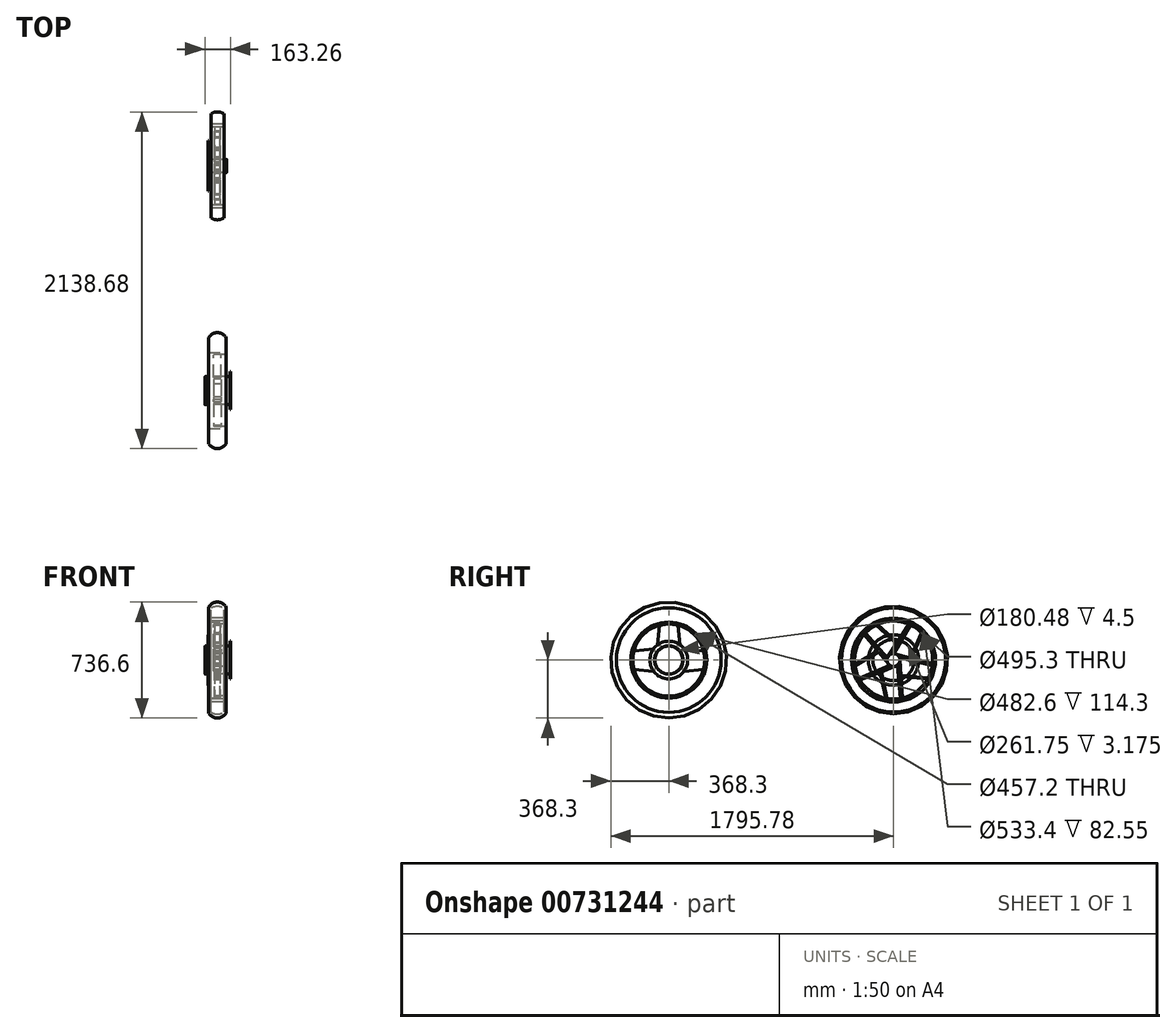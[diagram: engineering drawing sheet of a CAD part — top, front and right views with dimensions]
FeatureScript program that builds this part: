
annotation { "Feature Type Name" : "Feature", "Feature Type Description" : "" }
export const myFeature = defineFeature(function(context is Context, id is Id, definition is map)
    precondition{}
    {
        {
            var Q0;
            Q0=qCreatedBy(makeId("Right.planeOp"),FACE);
            var sketch = newSketch(context, id + "F0", { "sketchPlane" : qUnion([Q0])});
            skCircle(sketch, "E0", {"center": v(0, 0) * mm, "radius": 247.65 * mm});
            skCircle(sketch, "E1", {"center": v(0, 0) * mm, "radius": 41.28 * mm});
            skLineSegment(sketch, "E2", {"start": v(55.3, -241.4) * mm, "end": v(47.4, -104.93) * mm});
            skLineSegment(sketch, "E3", {"start": v(46.96, -97.18) * mm, "end": v(219.73, -114.22) * mm});
            skLineSegment(sketch, "E4.1.0", {"start": v(246.67, -22) * mm, "end": v(114.45, 12.66) * mm});
            skLineSegment(sketch, "E4.1.1", {"start": v(106.93, 14.63) * mm, "end": v(176.54, 173.68) * mm});
            skLineSegment(sketch, "E4.2.0", {"start": v(97.16, 227.8) * mm, "end": v(23.33, 112.76) * mm});
            skLineSegment(sketch, "E4.2.1", {"start": v(19.13, 106.22) * mm, "end": v(-110.63, 221.57) * mm});
            skLineSegment(sketch, "E4.3.0", {"start": v(-186.62, 162.8) * mm, "end": v(-100.03, 57.03) * mm});
            skLineSegment(sketch, "E4.3.1", {"start": v(-95.1, 51.01) * mm, "end": v(-244.9, -36.75) * mm});
            skLineSegment(sketch, "E4.4.0", {"start": v(-212.5, -127.18) * mm, "end": v(-85.15, -77.51) * mm});
            skLineSegment(sketch, "E4.4.1", {"start": v(-77.9, -74.7) * mm, "end": v(-40.73, -244.28) * mm});
            skLineSegment(sketch, "E5", {"start": v(43.26, -243.84) * mm, "end": v(23.46, -33.96) * mm});
            skLineSegment(sketch, "E6", {"start": v(47.4, -104.93) * mm, "end": v(215.77, -121.55) * mm});
            skLineSegment(sketch, "E7.1.0", {"start": v(245.28, -34.2) * mm, "end": v(39.55, 11.82) * mm});
            skLineSegment(sketch, "E7.1.1", {"start": v(114.45, 12.66) * mm, "end": v(182.28, 167.65) * mm});
            skLineSegment(sketch, "E7.2.0", {"start": v(108.33, 222.7) * mm, "end": v(0.98, 41.26) * mm});
            skLineSegment(sketch, "E7.2.1", {"start": v(23.33, 112.76) * mm, "end": v(-103.12, 225.16) * mm});
            skLineSegment(sketch, "E7.3.0", {"start": v(-178.33, 171.84) * mm, "end": v(-38.94, 13.68) * mm});
            skLineSegment(sketch, "E7.3.1", {"start": v(-100.03, 57.03) * mm, "end": v(-246, -28.5) * mm});
            skLineSegment(sketch, "E7.4.0", {"start": v(-218.54, -116.5) * mm, "end": v(-25.05, -32.8) * mm});
            skLineSegment(sketch, "E7.4.1", {"start": v(-85.15, -77.51) * mm, "end": v(-48.92, -242.77) * mm});
            skLineSegment(sketch, "E8.trimOffspring", {"start": v(19.13, 106.22) * mm, "end": v(-34.74, 22.3) * mm});
            skLineSegment(sketch, "E9.trimOffspring", {"start": v(106.93, 14.63) * mm, "end": v(10.47, 39.93) * mm});
            skLineSegment(sketch, "E10.trimOffspring", {"start": v(46.96, -97.18) * mm, "end": v(41.2, 2.38) * mm});
            skLineSegment(sketch, "E11.trimOffspring", {"start": v(-77.9, -74.7) * mm, "end": v(15, -38.45) * mm});
            skLineSegment(sketch, "E12.trimOffspring", {"start": v(-95.1, 51.01) * mm, "end": v(-31.94, -26.15) * mm});
            skCircle(sketch, "E13", {"center": v(0, 0) * mm, "radius": 266.7 * mm});
            skPoint(sketch, "E14.orphan", {"position": v(246.67, -22) * mm});
            skPoint(sketch, "E15.orphan", {"position": v(245.28, -34.2) * mm});
            skPoint(sketch, "E16.orphan", {"position": v(182.28, 167.65) * mm});
            skPoint(sketch, "E17.orphan", {"position": v(176.54, 173.68) * mm});
            skPoint(sketch, "E18.orphan", {"position": v(108.33, 222.7) * mm});
            skPoint(sketch, "E19.orphan", {"position": v(97.16, 227.8) * mm});
            skPoint(sketch, "E20.orphan", {"position": v(-103.12, 225.16) * mm});
            skPoint(sketch, "E21.orphan", {"position": v(-110.63, 221.57) * mm});
            skPoint(sketch, "E22.orphan", {"position": v(-178.33, 171.84) * mm});
            skPoint(sketch, "E23.orphan", {"position": v(-186.62, 162.8) * mm});
            skPoint(sketch, "E24.orphan", {"position": v(-246, -28.5) * mm});
            skPoint(sketch, "E25.orphan", {"position": v(-244.9, -36.75) * mm});
            skPoint(sketch, "E26.orphan", {"position": v(-218.54, -116.5) * mm});
            skPoint(sketch, "E27.orphan", {"position": v(-212.5, -127.18) * mm});
            skPoint(sketch, "E28.orphan", {"position": v(-48.92, -242.77) * mm});
            skPoint(sketch, "E29.orphan", {"position": v(-40.73, -244.28) * mm});
            skPoint(sketch, "E30.orphan", {"position": v(12.78, 39.32) * mm});
            skPoint(sketch, "E31.orphan", {"position": v(-33.45, 24.3) * mm});
            skPoint(sketch, "E32.orphan", {"position": v(-33.45, -24.3) * mm});
            skPoint(sketch, "E33.orphan", {"position": v(12.78, -39.32) * mm});
            skPoint(sketch, "E34.orphan", {"position": v(41.34, 0) * mm});
            skCircle(sketch, "E35", {"center": v(48.96, -107.55) * mm, "radius": 12.7 * mm, "construction": true});
            skPoint(sketch, "E35.first.point", {"position": v(61.6, -106.34) * mm});
            skPoint(sketch, "E35.second.point", {"position": v(47.58, -120.18) * mm});
            skPoint(sketch, "E35.third.point", {"position": v(38.36, -100.56) * mm});
            skCircle(sketch, "E36.1.0", {"center": v(117.42, 13.33) * mm, "radius": 12.7 * mm, "construction": true});
            skCircle(sketch, "E36.2.0", {"center": v(23.6, 115.8) * mm, "radius": 12.7 * mm, "construction": true});
            skCircle(sketch, "E36.3.0", {"center": v(-102.83, 58.23) * mm, "radius": 12.7 * mm, "construction": true});
            skCircle(sketch, "E36.4.0", {"center": v(-87.16, -79.8) * mm, "radius": 12.7 * mm, "construction": true});
            skCircle(sketch, "E37", {"center": v(0, 0) * mm, "radius": 342.9 * mm});
            skLineSegment(sketch, "E38", {"start": v(0, 0) * mm, "end": v(342.9, 1.85) * mm, "construction": true});
            skLineSegment(sketch, "E39", {"start": v(0, -342.9) * mm, "end": v(0, 342.9) * mm, "construction": true});
            skSolve(sketch);
        }
        {
            var Q0;
            Q0=qCreatedBy(makeId("Right.planeOp"),FACE);
            cPlane(context, id + "F1", {"entities" : qUnion([Q0]), "cplaneType" : CPlaneType.OFFSET, "offset" : 60.32 * mm, "oppositeDirection" : true, "width" : 152.4 * mm, "height" : 152.4 * mm});
        }
        {
            var Q0;
            Q0=qCreatedBy(id+"F1.planeOp",FACE);
            var sketch = newSketch(context, id + "F2", { "sketchPlane" : qUnion([Q0])});
            skCircle(sketch, "E40.0", {"center": v(48.96, -107.55) * mm, "radius": 12.7 * mm});
            skCircle(sketch, "E41.0", {"center": v(117.42, 13.33) * mm, "radius": 12.7 * mm});
            skCircle(sketch, "E42.0", {"center": v(23.6, 115.8) * mm, "radius": 12.7 * mm});
            skCircle(sketch, "E43.0", {"center": v(-102.83, 58.23) * mm, "radius": 12.7 * mm});
            skCircle(sketch, "E44.0", {"center": v(-87.16, -79.8) * mm, "radius": 12.7 * mm});
            skPoint(sketch, "E45.0", {"position": v(0, 0) * mm});
            skCircle(sketch, "E46", {"center": v(0, 0) * mm, "radius": 130.87 * mm});
            skCircle(sketch, "E47", {"center": v(0, 0) * mm, "radius": 160 * mm});
            skSolve(sketch);
        }
        {
            var Q0;
            {var subQ0=sQuery(id+"F0.wireOp",EDGE,"E1");var subQ5=makeQuery(id+"F0.imprint","INTERSECT",VERTEX,{"derivedFrom":[subQ0,sQuery(id+"F0.wireOp",EDGE,"E7.1.0")]});Q0=makeQuery(id+"F0.imprint","IMPRINT",FACE,{"disambiguationData":[TD([[makeQuery(id+"F0.imprint","IMPRINT",EDGE,{"disambiguationData":[TD([[subQ5,-1.0]])],"derivedFrom":subQ0}),1.0]])]});}
            extrude(context, id + "F3", {"entities" : qUnion([Q0]), "endBound" : BoundingType.SYMMETRIC, "depth" : 120.65 * mm});
        }
        {
            var Q0;
            Q0=makeQuery(id+"F0.imprint","IMPRINT",FACE,{"disambiguationData":[TD([[makeQuery(id+"F0.imprint","IMPRINT",EDGE,{"derivedFrom":sQuery(id+"F0.wireOp",EDGE,"E13")}),1.0]])]});
            extrude(context, id + "F4", {"entities" : qUnion([Q0]), "endBound" : BoundingType.SYMMETRIC, "depth" : 82.55 * mm});
        }
        {
            var Q0;
            {var subQ0=sQuery(id+"F0.wireOp",EDGE,"E2");Q0=makeQuery(id+"F0.imprint","IMPRINT",FACE,{"disambiguationData":[TD([[makeQuery(id+"F0.imprint","IMPRINT",EDGE,{"derivedFrom":subQ0}),1.0]])]});}
            var Q1;
            {var subQ0=sQuery(id+"F0.wireOp",EDGE,"E4.1.0");Q1=makeQuery(id+"F0.imprint","IMPRINT",FACE,{"disambiguationData":[TD([[makeQuery(id+"F0.imprint","IMPRINT",EDGE,{"derivedFrom":subQ0}),1.0]])]});}
            var Q2;
            {var subQ3=sQuery(id+"F0.wireOp",EDGE,"E4.2.0");Q2=makeQuery(id+"F0.imprint","IMPRINT",FACE,{"disambiguationData":[TD([[makeQuery(id+"F0.imprint","IMPRINT",EDGE,{"derivedFrom":subQ3}),1.0]])]});}
            var Q3;
            {var subQ3=sQuery(id+"F0.wireOp",EDGE,"E4.3.0");Q3=makeQuery(id+"F0.imprint","IMPRINT",FACE,{"disambiguationData":[TD([[makeQuery(id+"F0.imprint","IMPRINT",EDGE,{"derivedFrom":subQ3}),1.0]])]});}
            var Q4;
            {var subQ0=sQuery(id+"F0.wireOp",EDGE,"E4.4.0");Q4=makeQuery(id+"F0.imprint","IMPRINT",FACE,{"disambiguationData":[TD([[makeQuery(id+"F0.imprint","IMPRINT",EDGE,{"derivedFrom":subQ0}),1.0]])]});}
            extrude(context, id + "F5", {"entities" : qUnion([Q0, Q1, Q2, Q3, Q4]), "endBound" : BoundingType.SYMMETRIC, "depth" : 34.92 * mm});
        }
        {
            var Q0;
            Q0=qCreatedBy(makeId("Top.planeOp"),FACE);
            var sketch = newSketch(context, id + "F6", { "sketchPlane" : qUnion([Q0])});
            skPoint(sketch, "E48.0", {"position": v(0, 342.9) * mm});
            skLineSegment(sketch, "E49", {"start": v(-41.28, 266.7) * mm, "end": v(41.28, 266.7) * mm});
            skLineSegment(sketch, "E50", {"start": v(-41.28, 266.7) * mm, "end": v(-41.28, 330.75) * mm});
            skLineSegment(sketch, "E51", {"start": v(41.28, 266.7) * mm, "end": v(41.28, 330.75) * mm});
            skPoint(sketch, "E52", {"position": v(0, 266.7) * mm});
            skArc(sketch, "E53", {"start": v(-41.27, 330.75) * mm, "mid": v(0, 342.9) * mm, "end": v(41.27, 330.75) * mm});
            skPoint(sketch, "E54.orphan", {"position": v(-41.28, 342.9) * mm});
            skPoint(sketch, "E55.orphan", {"position": v(41.28, 342.9) * mm});
            skLineSegment(sketch, "E56", {"start": v(0, 0) * mm, "end": v(-156.28, 0) * mm, "construction": true});
            skSolve(sketch);
        }
        {
            var Q0;
            Q0=makeQuery(id+"F6.imprint","IMPRINT",FACE,{"disambiguationData":[TD([[makeQuery(id+"F6.imprint","IMPRINT",EDGE,{"derivedFrom":sQuery(id+"F6.wireOp",EDGE,"E49")}),1.0]])]});
            var Q1;
            Q1=sQuery(id+"F6.wireOp",EDGE,"E56");
            revolve(context, id + "F7", {"entities" : qUnion([Q0]), "axis" : qUnion([Q1]), "revolveType" : RevolveType.FULL});
        }
        {
            var Q0;
            Q0=qCreatedBy(makeId("Right.planeOp"),FACE);
            cPlane(context, id + "F8", {"entities" : qUnion([Q0]), "cplaneType" : CPlaneType.OFFSET, "offset" : 38.1 * mm, "width" : 152.4 * mm, "height" : 152.4 * mm});
        }
        {
            var Q0;
            Q0=qCreatedBy(id+"F8.planeOp",FACE);
            var sketch = newSketch(context, id + "F9", { "sketchPlane" : qUnion([Q0])});
            skArc(sketch, "E57", {"start": v(239.96, 25.4) * mm, "mid": v(-241.3, 0) * mm, "end": v(239.96, -25.4) * mm});
            skArc(sketch, "E58", {"start": v(28.4, 25.4) * mm, "mid": v(-38.1, 0) * mm, "end": v(28.4, -25.4) * mm});
            skLineSegment(sketch, "E59", {"start": v(28.4, 25.4) * mm, "end": v(239.96, 25.4) * mm});
            skLineSegment(sketch, "E60", {"start": v(28.4, -25.4) * mm, "end": v(239.96, -25.4) * mm});
            skSolve(sketch);
        }
        {
            var Q0;
            Q0=qCreatedBy(makeId("Right.planeOp"),FACE);
            cPlane(context, id + "F10", {"entities" : qUnion([Q0]), "cplaneType" : CPlaneType.OFFSET, "offset" : 38.1 * mm, "oppositeDirection" : true, "width" : 152.4 * mm, "height" : 152.4 * mm});
        }
        {
            var Q0;
            Q0=qCreatedBy(id+"F10.planeOp",FACE);
            var sketch = newSketch(context, id + "F11", { "sketchPlane" : qUnion([Q0])});
            skCircle(sketch, "E61", {"center": v(0, 0) * mm, "radius": 241.3 * mm});
            skArc(sketch, "E62", {"start": v(25.3, 137.4) * mm, "mid": v(0, 165.1) * mm, "end": v(-25.3, 137.4) * mm});
            skArc(sketch, "E63.1.0", {"start": v(-122.85, 66.51) * mm, "mid": v(-157.02, 51.02) * mm, "end": v(-138.48, 18.4) * mm});
            skArc(sketch, "E63.2.0", {"start": v(-101.22, -96.28) * mm, "mid": v(-97.04, -133.57) * mm, "end": v(-60.3, -126.02) * mm});
            skArc(sketch, "E63.3.0", {"start": v(60.3, -126.02) * mm, "mid": v(97.04, -133.57) * mm, "end": v(101.22, -96.28) * mm});
            skArc(sketch, "E63.4.0", {"start": v(138.48, 18.4) * mm, "mid": v(157.02, 51.02) * mm, "end": v(122.85, 66.51) * mm});
            skArc(sketch, "E64", {"start": v(28, 25.83) * mm, "mid": v(22.4, 30.82) * mm, "end": v(15.91, 34.62) * mm});
            skLineSegment(sketch, "E65", {"start": v(101.22, -96.28) * mm, "end": v(33.22, -18.65) * mm});
            skLineSegment(sketch, "E66", {"start": v(138.48, 18.4) * mm, "end": v(37.84, -4.44) * mm});
            skLineSegment(sketch, "E67", {"start": v(122.85, 66.51) * mm, "end": v(28, 25.83) * mm});
            skLineSegment(sketch, "E68", {"start": v(25.3, 137.4) * mm, "end": v(15.91, 34.62) * mm});
            skLineSegment(sketch, "E69", {"start": v(-25.3, 137.4) * mm, "end": v(-15.91, 34.62) * mm});
            skLineSegment(sketch, "E70", {"start": v(-122.85, 66.51) * mm, "end": v(-28, 25.83) * mm});
            skLineSegment(sketch, "E71", {"start": v(-138.48, 18.4) * mm, "end": v(-37.84, -4.44) * mm});
            skLineSegment(sketch, "E72", {"start": v(-101.22, -96.28) * mm, "end": v(-33.22, -18.65) * mm});
            skLineSegment(sketch, "E73", {"start": v(-60.3, -126.02) * mm, "end": v(-7.47, -37.36) * mm});
            skLineSegment(sketch, "E74", {"start": v(60.3, -126.02) * mm, "end": v(7.47, -37.36) * mm});
            skArc(sketch, "E75.trimOffspring", {"start": v(33.22, -18.65) * mm, "mid": v(36.24, -11.77) * mm, "end": v(37.84, -4.44) * mm});
            skArc(sketch, "E76.trimOffspring", {"start": v(-7.47, -37.36) * mm, "mid": v(0, -38.1) * mm, "end": v(7.47, -37.36) * mm});
            skArc(sketch, "E77.trimOffspring", {"start": v(-37.84, -4.44) * mm, "mid": v(-36.24, -11.77) * mm, "end": v(-33.22, -18.65) * mm});
            skArc(sketch, "E78.trimOffspring", {"start": v(-15.91, 34.62) * mm, "mid": v(-22.4, 30.82) * mm, "end": v(-28, 25.83) * mm});
            skSolve(sketch);
        }
        {
            var Q0;
            Q0=qCreatedBy(makeId("Right.planeOp"),FACE);
            var sketch = newSketch(context, id + "F12", { "sketchPlane" : qUnion([Q0])});
            skCircle(sketch, "E79", {"center": v(-1427.48, 0) * mm, "radius": 228.6 * mm});
            skCircle(sketch, "E80", {"center": v(-1427.48, 0) * mm, "radius": 88.9 * mm});
            skCircle(sketch, "E81", {"center": v(-1427.48, 0) * mm, "radius": 241.3 * mm});
            skLineSegment(sketch, "E82", {"start": v(-1427.48, 0) * mm, "end": v(-1059.18, 0) * mm, "construction": true});
            skCircle(sketch, "E83", {"center": v(-1427.48, 0) * mm, "radius": 368.3 * mm});
            skLineSegment(sketch, "E84.1.0", {"start": v(-1427.48, 0) * mm, "end": v(-1167.05, 260.43) * mm, "construction": true});
            skLineSegment(sketch, "E84.2.0", {"start": v(-1427.48, 0) * mm, "end": v(-1427.48, 368.3) * mm, "construction": true});
            skLineSegment(sketch, "E84.3.0", {"start": v(-1427.48, 0) * mm, "end": v(-1687.9, 260.43) * mm, "construction": true});
            skLineSegment(sketch, "E84.4.0", {"start": v(-1427.48, 0) * mm, "end": v(-1795.78, 0) * mm, "construction": true});
            skLineSegment(sketch, "E84.5.0", {"start": v(-1427.48, 0) * mm, "end": v(-1687.9, -260.43) * mm, "construction": true});
            skLineSegment(sketch, "E84.6.0", {"start": v(-1427.48, 0) * mm, "end": v(-1427.48, -368.3) * mm, "construction": true});
            skLineSegment(sketch, "E84.7.0", {"start": v(-1427.48, 0) * mm, "end": v(-1167.05, -260.43) * mm, "construction": true});
            skPoint(sketch, "E85", {"position": v(-1348.62, -78.86) * mm});
            skArc(sketch, "E86", {"start": v(-1348.62, -41.05) * mm, "mid": v(-1338.6, -55.45) * mm, "end": v(-1339.53, -72.97) * mm});
            skLineSegment(sketch, "E87", {"start": v(-1345.5, -81.99) * mm, "end": v(-1360.73, -218.64) * mm});
            skLineSegment(sketch, "E88", {"start": v(-1354.51, -87.95) * mm, "end": v(-1369.36, -221.09) * mm});
            skLineSegment(sketch, "E89.MirrorCS", {"start": v(-1345.5, -81.99) * mm, "end": v(-1208.84, -66.75) * mm});
            skLineSegment(sketch, "E90.MirrorCS", {"start": v(-1339.53, -72.97) * mm, "end": v(-1206.4, -58.12) * mm});
            skPoint(sketch, "E91.orphan", {"position": v(-1206.4, -58.12) * mm});
            skPoint(sketch, "E92.orphan", {"position": v(-1208.84, -66.75) * mm});
            skPoint(sketch, "E93.orphan", {"position": v(-1339.53, -72.97) * mm});
            skPoint(sketch, "E94.orphan", {"position": v(-1345.5, -81.99) * mm});
            skArc(sketch, "E95.trimOffspring", {"start": v(-1354.51, -87.95) * mm, "mid": v(-1372.03, -88.87) * mm, "end": v(-1386.43, -78.86) * mm});
            skArc(sketch, "E96.1.0", {"start": v(-1339.53, 72.97) * mm, "mid": v(-1338.6, 55.45) * mm, "end": v(-1348.62, 41.05) * mm});
            skLineSegment(sketch, "E96.1.1", {"start": v(-1339.53, 72.97) * mm, "end": v(-1206.4, 58.12) * mm});
            skLineSegment(sketch, "E96.1.2", {"start": v(-1345.5, 81.99) * mm, "end": v(-1208.84, 66.75) * mm});
            skLineSegment(sketch, "E96.1.3", {"start": v(-1345.5, 81.99) * mm, "end": v(-1360.73, 218.64) * mm});
            skLineSegment(sketch, "E96.1.4", {"start": v(-1354.51, 87.95) * mm, "end": v(-1369.36, 221.09) * mm});
            skArc(sketch, "E96.1.5", {"start": v(-1386.43, 78.86) * mm, "mid": v(-1372.03, 88.87) * mm, "end": v(-1354.51, 87.95) * mm});
            skArc(sketch, "E96.2.0", {"start": v(-1500.45, 87.95) * mm, "mid": v(-1482.93, 88.87) * mm, "end": v(-1468.53, 78.86) * mm});
            skLineSegment(sketch, "E96.2.1", {"start": v(-1500.45, 87.95) * mm, "end": v(-1485.6, 221.09) * mm});
            skLineSegment(sketch, "E96.2.2", {"start": v(-1509.47, 81.99) * mm, "end": v(-1494.23, 218.64) * mm});
            skLineSegment(sketch, "E96.2.3", {"start": v(-1509.47, 81.99) * mm, "end": v(-1646.12, 66.75) * mm});
            skLineSegment(sketch, "E96.2.4", {"start": v(-1515.43, 72.97) * mm, "end": v(-1648.57, 58.12) * mm});
            skArc(sketch, "E96.2.5", {"start": v(-1506.34, 41.05) * mm, "mid": v(-1516.35, 55.45) * mm, "end": v(-1515.43, 72.97) * mm});
            skArc(sketch, "E96.3.0", {"start": v(-1515.43, -72.97) * mm, "mid": v(-1516.35, -55.45) * mm, "end": v(-1506.34, -41.05) * mm});
            skLineSegment(sketch, "E96.3.1", {"start": v(-1515.43, -72.97) * mm, "end": v(-1648.57, -58.12) * mm});
            skLineSegment(sketch, "E96.3.2", {"start": v(-1509.47, -81.99) * mm, "end": v(-1646.12, -66.75) * mm});
            skLineSegment(sketch, "E96.3.3", {"start": v(-1509.47, -81.99) * mm, "end": v(-1494.23, -218.64) * mm});
            skLineSegment(sketch, "E96.3.4", {"start": v(-1500.45, -87.95) * mm, "end": v(-1485.6, -221.09) * mm});
            skArc(sketch, "E96.3.5", {"start": v(-1468.53, -78.86) * mm, "mid": v(-1482.93, -88.87) * mm, "end": v(-1500.45, -87.95) * mm});
            skSolve(sketch);
        }
        {
            var Q0;
            Q0=makeQuery(id+"F12.imprint","IMPRINT",FACE,{"disambiguationData":[TD([[makeQuery(id+"F12.imprint","IMPRINT",EDGE,{"derivedFrom":sQuery(id+"F12.wireOp",EDGE,"E79")}),-1.0]])]});
            var Q1;
            Q1=sQuery(id+"F12.wireOp",EDGE,"E79");
            extrude(context, id + "F13", {"entities" : qUnion([Q0]), "surfaceEntities" : qUnion([Q1]), "endBound" : BoundingType.SYMMETRIC, "depth" : 114.3 * mm});
        }
        {
            var Q0;
            Q0=makeQuery(id+"F12.imprint","IMPRINT",FACE,{"disambiguationData":[TD([[makeQuery(id+"F12.imprint","IMPRINT",EDGE,{"derivedFrom":sQuery(id+"F12.wireOp",EDGE,"E80")}),1.0]])]});
            var Q1;
            Q1=sQuery(id+"F12.wireOp",EDGE,"E80");
            extrude(context, id + "F14", {"entities" : qUnion([Q0]), "surfaceEntities" : qUnion([Q1]), "endBound" : BoundingType.SYMMETRIC, "depth" : 158.75 * mm});
        }
        {
            var Q0;
            Q0=qSketchRegion(id+"F2",true);
            extrude(context, id + "F15", {"entities" : qUnion([Q0]), "depth" : 3.17 * mm});
        }
        {
            var Q0;
            Q0=sQuery(id+"F2.wireOp",EDGE,"E43.0");
            var Q1;
            Q1=sQuery(id+"F2.wireOp",EDGE,"E44.0");
            var Q2;
            Q2=sQuery(id+"F2.wireOp",EDGE,"E42.0");
            var Q3;
            Q3=sQuery(id+"F2.wireOp",EDGE,"E41.0");
            var Q4;
            Q4=sQuery(id+"F2.wireOp",EDGE,"E40.0");
            extrude(context, id + "F16", {"bodyType" : ToolBodyType.SURFACE, "surfaceEntities" : qUnion([Q0, Q1, Q2, Q3, Q4]), "depth" : 77.8 * mm});
        }
        {
            var Q0;
            Q0=makeQuery(id+"F5.opExtrude","CAP_FACE",FACE,{"disambiguationData":[OSD([sQuery(id+"F0.wireOp",EDGE,"E0"),sQuery(id+"F0.wireOp",EDGE,"E1"),sQuery(id+"F0.wireOp",EDGE,"E4.3.0"),sQuery(id+"F0.wireOp",EDGE,"E4.3.1"),sQuery(id+"F0.wireOp",EDGE,"E7.3.0"),sQuery(id+"F0.wireOp",EDGE,"E7.3.1"),sQuery(id+"F0.wireOp",EDGE,"E12.trimOffspring")])],"isStart":false});
            var Q1;
            Q1=makeQuery(id+"F5.opExtrude","CAP_FACE",FACE,{"disambiguationData":[OSD([sQuery(id+"F0.wireOp",EDGE,"E0"),sQuery(id+"F0.wireOp",EDGE,"E1"),sQuery(id+"F0.wireOp",EDGE,"E4.2.0"),sQuery(id+"F0.wireOp",EDGE,"E4.2.1"),sQuery(id+"F0.wireOp",EDGE,"E7.2.0"),sQuery(id+"F0.wireOp",EDGE,"E7.2.1"),sQuery(id+"F0.wireOp",EDGE,"E8.trimOffspring")])],"isStart":false});
            var Q2;
            Q2=makeQuery(id+"F5.opExtrude","CAP_FACE",FACE,{"disambiguationData":[OSD([sQuery(id+"F0.wireOp",EDGE,"E0"),sQuery(id+"F0.wireOp",EDGE,"E1"),sQuery(id+"F0.wireOp",EDGE,"E4.1.0"),sQuery(id+"F0.wireOp",EDGE,"E4.1.1"),sQuery(id+"F0.wireOp",EDGE,"E7.1.0"),sQuery(id+"F0.wireOp",EDGE,"E7.1.1"),sQuery(id+"F0.wireOp",EDGE,"E9.trimOffspring")])],"isStart":false});
            var Q3;
            Q3=makeQuery(id+"F5.opExtrude","CAP_FACE",FACE,{"disambiguationData":[OSD([sQuery(id+"F0.wireOp",EDGE,"E0"),sQuery(id+"F0.wireOp",EDGE,"E1"),sQuery(id+"F0.wireOp",EDGE,"E2"),sQuery(id+"F0.wireOp",EDGE,"E3"),sQuery(id+"F0.wireOp",EDGE,"E5"),sQuery(id+"F0.wireOp",EDGE,"E6"),sQuery(id+"F0.wireOp",EDGE,"E10.trimOffspring")])],"isStart":false});
            var Q4;
            Q4=makeQuery(id+"F5.opExtrude","CAP_FACE",FACE,{"disambiguationData":[OSD([sQuery(id+"F0.wireOp",EDGE,"E0"),sQuery(id+"F0.wireOp",EDGE,"E1"),sQuery(id+"F0.wireOp",EDGE,"E4.4.0"),sQuery(id+"F0.wireOp",EDGE,"E4.4.1"),sQuery(id+"F0.wireOp",EDGE,"E7.4.0"),sQuery(id+"F0.wireOp",EDGE,"E7.4.1"),sQuery(id+"F0.wireOp",EDGE,"E11.trimOffspring")])],"isStart":false});
            var Q5;
            Q5=makeQuery(id+"F3.opExtrude","SWEPT_FACE",FACE,{"disambiguationData":[OSD([sQuery(id+"F0.wireOp",EDGE,"E1")])]});
            var Q6;
            Q6=makeQuery(id+"F16.opExtrude","SWEPT_FACE",FACE,{"disambiguationData":[OSD([sQuery(id+"F2.wireOp",EDGE,"E41.0")])]});
            var Q7;
            Q7=makeQuery(id+"F16.opExtrude","SWEPT_FACE",FACE,{"disambiguationData":[OSD([sQuery(id+"F2.wireOp",EDGE,"E42.0")])]});
            var Q8;
            Q8=makeQuery(id+"F16.opExtrude","SWEPT_FACE",FACE,{"disambiguationData":[OSD([sQuery(id+"F2.wireOp",EDGE,"E43.0")])]});
            var Q9;
            Q9=makeQuery(id+"F16.opExtrude","SWEPT_FACE",FACE,{"disambiguationData":[OSD([sQuery(id+"F2.wireOp",EDGE,"E44.0")])]});
            var Q10;
            Q10=makeQuery(id+"F16.opExtrude","SWEPT_FACE",FACE,{"disambiguationData":[OSD([sQuery(id+"F2.wireOp",EDGE,"E40.0")])]});
            var Q11;
            Q11=makeQuery(id+"F4.opExtrude","SWEPT_FACE",FACE,{"disambiguationData":[OSD([sQuery(id+"F0.wireOp",EDGE,"E0")])]});
            fillet(context, id + "F17", {"entities" : qUnion([Q0, Q1, Q2, Q3, Q4, Q5, Q6, Q7, Q8, Q9, Q10, Q11]), "radius" : 2.54 * mm, "tangentPropagation" : true, "allowEdgeOverflow" : false});
        }
        {
            var Q0;
            Q0=qCreatedBy(makeId("Top.planeOp"),FACE);
            var sketch = newSketch(context, id + "F18", { "sketchPlane" : qUnion([Q0])});
            skLineSegment(sketch, "E97", {"start": v(-57.15, -1186.18) * mm, "end": v(57.15, -1186.18) * mm});
            skLineSegment(sketch, "E98.0", {"start": v(0, -1059.18) * mm, "end": v(0, -1795.78) * mm, "construction": true});
            skLineSegment(sketch, "E99", {"start": v(-57.15, -1186.18) * mm, "end": v(-57.15, -1095.04) * mm});
            skLineSegment(sketch, "E100.MirrorCS", {"start": v(57.15, -1186.18) * mm, "end": v(57.15, -1095.04) * mm});
            skLineSegment(sketch, "E101", {"start": v(-57.15, -1095.04) * mm, "end": v(57.15, -1095.04) * mm, "construction": true});
            skPoint(sketch, "E102.orphan", {"position": v(57.15, -1059.18) * mm});
            skPoint(sketch, "E103.orphan", {"position": v(-57.15, -1059.18) * mm});
            skArc(sketch, "E104", {"start": v(57.15, -1095.04) * mm, "mid": v(0, -1059.18) * mm, "end": v(-57.15, -1095.04) * mm});
            skPoint(sketch, "E105.0", {"position": v(0, -1427.48) * mm});
            skLineSegment(sketch, "E106", {"start": v(0, -1427.48) * mm, "end": v(-122.3, -1427.48) * mm, "construction": true});
            skLineSegment(sketch, "E107", {"start": v(57.15, -1186.18) * mm, "end": v(-57.15, -1186.18) * mm});
            skSolve(sketch);
        }
        {
            var Q0;
            {var subQ0=sQuery(id+"F12.wireOp",EDGE,"E96.2.0");Q0=makeQuery(id+"F12.imprint","IMPRINT",FACE,{"disambiguationData":[TD([[makeQuery(id+"F12.imprint","IMPRINT",EDGE,{"derivedFrom":subQ0}),-1.0]])]});}
            var Q1;
            {var subQ0=sQuery(id+"F12.wireOp",EDGE,"E96.1.0");Q1=makeQuery(id+"F12.imprint","IMPRINT",FACE,{"disambiguationData":[TD([[makeQuery(id+"F12.imprint","IMPRINT",EDGE,{"derivedFrom":subQ0}),-1.0]])]});}
            var Q2;
            {var subQ0=sQuery(id+"F12.wireOp",EDGE,"E86");Q2=makeQuery(id+"F12.imprint","IMPRINT",FACE,{"disambiguationData":[TD([[makeQuery(id+"F12.imprint","IMPRINT",EDGE,{"derivedFrom":subQ0}),-1.0]])]});}
            var Q3;
            {var subQ0=sQuery(id+"F12.wireOp",EDGE,"E96.3.0");Q3=makeQuery(id+"F12.imprint","IMPRINT",FACE,{"disambiguationData":[TD([[makeQuery(id+"F12.imprint","IMPRINT",EDGE,{"derivedFrom":subQ0}),-1.0]])]});}
            extrude(context, id + "F19", {"entities" : qUnion([Q0, Q1, Q2, Q3]), "endBound" : BoundingType.SYMMETRIC, "depth" : 44.45 * mm});
        }
        {
            var Q0;
            Q0=makeQuery(id+"F18.imprint","IMPRINT",FACE,{"disambiguationData":[TD([[makeQuery(id+"F18.imprint","IMPRINT",EDGE,{"derivedFrom":sQuery(id+"F18.wireOp",EDGE,"E99")}),-1.0]])]});
            var Q1;
            Q1=sQuery(id+"F18.wireOp",EDGE,"E106");
            revolve(context, id + "F20", {"entities" : qUnion([Q0]), "axis" : qUnion([Q1]), "revolveType" : RevolveType.FULL});
        }
        {
            var Q0;
            Q0=qCreatedBy(makeId("Right.planeOp"),FACE);
            cPlane(context, id + "F21", {"entities" : qUnion([Q0]), "cplaneType" : CPlaneType.OFFSET, "offset" : 79.38 * mm, "width" : 152.4 * mm, "height" : 152.4 * mm});
        }
        {
            var Q0;
            Q0=qCreatedBy(id+"F21.planeOp",FACE);
            var sketch = newSketch(context, id + "F22", { "sketchPlane" : qUnion([Q0])});
            skPoint(sketch, "E108.0", {"position": v(-1427.48, 0) * mm});
            skCircle(sketch, "E109", {"center": v(-1427.48, 0) * mm, "radius": 120 * mm});
            skCircle(sketch, "E110", {"center": v(-1427.48, 0) * mm, "radius": 90.24 * mm});
            skSolve(sketch);
        }
        {
            var Q0;
            Q0=makeQuery(id+"F22.imprint","IMPRINT",FACE,{"disambiguationData":[TD([[makeQuery(id+"F22.imprint","IMPRINT",EDGE,{"derivedFrom":sQuery(id+"F22.wireOp",EDGE,"E109")}),1.0]])]});
            extrude(context, id + "F23", {"entities" : qUnion([Q0]), "depth" : 4.5 * mm});
        }
        {
            var Q0;
            Q0=makeQuery(id+"F14.opExtrude","SWEPT_FACE",FACE,{"disambiguationData":[OSD([sQuery(id+"F12.wireOp",EDGE,"E80")])]});
            var Q1;
            Q1=makeQuery(id+"F19.opExtrude","CAP_FACE",FACE,{"disambiguationData":[OSD([sQuery(id+"F12.wireOp",EDGE,"E79"),sQuery(id+"F12.wireOp",EDGE,"E80"),sQuery(id+"F12.wireOp",EDGE,"E96.2.0"),sQuery(id+"F12.wireOp",EDGE,"E96.2.1"),sQuery(id+"F12.wireOp",EDGE,"E96.2.2"),sQuery(id+"F12.wireOp",EDGE,"E96.2.3"),sQuery(id+"F12.wireOp",EDGE,"E96.2.4"),sQuery(id+"F12.wireOp",EDGE,"E96.2.5")])],"isStart":false});
            var Q2;
            Q2=makeQuery(id+"F19.opExtrude","SWEPT_FACE",FACE,{"disambiguationData":[OSD([sQuery(id+"F12.wireOp",EDGE,"E96.2.2")])]});
            var Q3;
            Q3=makeQuery(id+"F19.opExtrude","SWEPT_FACE",FACE,{"disambiguationData":[OSD([sQuery(id+"F12.wireOp",EDGE,"E96.2.3")])]});
            var Q4;
            Q4=makeQuery(id+"F19.opExtrude","SWEPT_FACE",FACE,{"disambiguationData":[OSD([sQuery(id+"F12.wireOp",EDGE,"E96.1.4")])]});
            var Q5;
            Q5=makeQuery(id+"F19.opExtrude","CAP_FACE",FACE,{"disambiguationData":[OSD([sQuery(id+"F12.wireOp",EDGE,"E79"),sQuery(id+"F12.wireOp",EDGE,"E80"),sQuery(id+"F12.wireOp",EDGE,"E96.1.0"),sQuery(id+"F12.wireOp",EDGE,"E96.1.1"),sQuery(id+"F12.wireOp",EDGE,"E96.1.2"),sQuery(id+"F12.wireOp",EDGE,"E96.1.3"),sQuery(id+"F12.wireOp",EDGE,"E96.1.4"),sQuery(id+"F12.wireOp",EDGE,"E96.1.5")])],"isStart":false});
            var Q6;
            Q6=makeQuery(id+"F19.opExtrude","SWEPT_FACE",FACE,{"disambiguationData":[OSD([sQuery(id+"F12.wireOp",EDGE,"E96.3.3")])]});
            var Q7;
            Q7=makeQuery(id+"F19.opExtrude","SWEPT_FACE",FACE,{"disambiguationData":[OSD([sQuery(id+"F12.wireOp",EDGE,"E96.3.2")])]});
            var Q8;
            Q8=makeQuery(id+"F19.opExtrude","CAP_FACE",FACE,{"disambiguationData":[OSD([sQuery(id+"F12.wireOp",EDGE,"E79"),sQuery(id+"F12.wireOp",EDGE,"E80"),sQuery(id+"F12.wireOp",EDGE,"E96.3.0"),sQuery(id+"F12.wireOp",EDGE,"E96.3.1"),sQuery(id+"F12.wireOp",EDGE,"E96.3.2"),sQuery(id+"F12.wireOp",EDGE,"E96.3.3"),sQuery(id+"F12.wireOp",EDGE,"E96.3.4"),sQuery(id+"F12.wireOp",EDGE,"E96.3.5")])],"isStart":false});
            var Q9;
            Q9=makeQuery(id+"F19.opExtrude","SWEPT_FACE",FACE,{"disambiguationData":[OSD([sQuery(id+"F12.wireOp",EDGE,"E88")])]});
            var Q10;
            Q10=makeQuery(id+"F19.opExtrude","CAP_FACE",FACE,{"disambiguationData":[OSD([sQuery(id+"F12.wireOp",EDGE,"E79"),sQuery(id+"F12.wireOp",EDGE,"E80"),sQuery(id+"F12.wireOp",EDGE,"E86"),sQuery(id+"F12.wireOp",EDGE,"E87"),sQuery(id+"F12.wireOp",EDGE,"E88"),sQuery(id+"F12.wireOp",EDGE,"E89.MirrorCS"),sQuery(id+"F12.wireOp",EDGE,"E90.MirrorCS"),sQuery(id+"F12.wireOp",EDGE,"E95.trimOffspring")])],"isStart":false});
            var Q11;
            Q11=makeQuery(id+"F19.opExtrude","SWEPT_FACE",FACE,{"disambiguationData":[OSD([sQuery(id+"F12.wireOp",EDGE,"E90.MirrorCS")])]});
            var Q12;
            Q12=makeQuery(id+"F19.opExtrude","SWEPT_FACE",FACE,{"disambiguationData":[OSD([sQuery(id+"F12.wireOp",EDGE,"E96.1.1")])]});
            var Q13;
            Q13=makeQuery(id+"F19.opExtrude","SWEPT_FACE",FACE,{"disambiguationData":[OSD([sQuery(id+"F12.wireOp",EDGE,"E86")])]});
            var Q14;
            Q14=makeQuery(id+"F19.opExtrude","SWEPT_FACE",FACE,{"disambiguationData":[OSD([sQuery(id+"F12.wireOp",EDGE,"E96.1.0")])]});
            var Q15;
            Q15=makeQuery(id+"F19.opExtrude","SWEPT_FACE",FACE,{"disambiguationData":[OSD([sQuery(id+"F12.wireOp",EDGE,"E96.3.5")])]});
            var Q16;
            Q16=makeQuery(id+"F13.opExtrude","SWEPT_FACE",FACE,{"disambiguationData":[OSD([sQuery(id+"F12.wireOp",EDGE,"E79")])]});
            var Q17;
            Q17=makeQuery(id+"F19.opExtrude","SWEPT_FACE",FACE,{"disambiguationData":[OSD([sQuery(id+"F12.wireOp",EDGE,"E96.2.4")])]});
            var Q18;
            Q18=makeQuery(id+"F19.opExtrude","CAP_FACE",FACE,{"disambiguationData":[OSD([sQuery(id+"F12.wireOp",EDGE,"E79"),sQuery(id+"F12.wireOp",EDGE,"E80"),sQuery(id+"F12.wireOp",EDGE,"E96.1.0"),sQuery(id+"F12.wireOp",EDGE,"E96.1.1"),sQuery(id+"F12.wireOp",EDGE,"E96.1.2"),sQuery(id+"F12.wireOp",EDGE,"E96.1.3"),sQuery(id+"F12.wireOp",EDGE,"E96.1.4"),sQuery(id+"F12.wireOp",EDGE,"E96.1.5")])],"isStart":true});
            var Q19;
            Q19=makeQuery(id+"F19.opExtrude","CAP_FACE",FACE,{"disambiguationData":[OSD([sQuery(id+"F12.wireOp",EDGE,"E79"),sQuery(id+"F12.wireOp",EDGE,"E80"),sQuery(id+"F12.wireOp",EDGE,"E86"),sQuery(id+"F12.wireOp",EDGE,"E87"),sQuery(id+"F12.wireOp",EDGE,"E88"),sQuery(id+"F12.wireOp",EDGE,"E89.MirrorCS"),sQuery(id+"F12.wireOp",EDGE,"E90.MirrorCS"),sQuery(id+"F12.wireOp",EDGE,"E95.trimOffspring")])],"isStart":true});
            var Q20;
            Q20=makeQuery(id+"F19.opExtrude","CAP_FACE",FACE,{"disambiguationData":[OSD([sQuery(id+"F12.wireOp",EDGE,"E79"),sQuery(id+"F12.wireOp",EDGE,"E80"),sQuery(id+"F12.wireOp",EDGE,"E96.2.0"),sQuery(id+"F12.wireOp",EDGE,"E96.2.1"),sQuery(id+"F12.wireOp",EDGE,"E96.2.2"),sQuery(id+"F12.wireOp",EDGE,"E96.2.3"),sQuery(id+"F12.wireOp",EDGE,"E96.2.4"),sQuery(id+"F12.wireOp",EDGE,"E96.2.5")])],"isStart":true});
            var Q21;
            Q21=makeQuery(id+"F19.opExtrude","CAP_FACE",FACE,{"disambiguationData":[OSD([sQuery(id+"F12.wireOp",EDGE,"E79"),sQuery(id+"F12.wireOp",EDGE,"E80"),sQuery(id+"F12.wireOp",EDGE,"E96.3.0"),sQuery(id+"F12.wireOp",EDGE,"E96.3.1"),sQuery(id+"F12.wireOp",EDGE,"E96.3.2"),sQuery(id+"F12.wireOp",EDGE,"E96.3.3"),sQuery(id+"F12.wireOp",EDGE,"E96.3.4"),sQuery(id+"F12.wireOp",EDGE,"E96.3.5")])],"isStart":true});
            fillet(context, id + "F24", {"entities" : qUnion([Q0, Q1, Q2, Q3, Q4, Q5, Q6, Q7, Q8, Q9, Q10, Q11, Q12, Q13, Q14, Q15, Q16, Q17, Q18, Q19, Q20, Q21]), "radius" : 2.54 * mm, "tangentPropagation" : true, "allowEdgeOverflow" : false});
        }
    });
